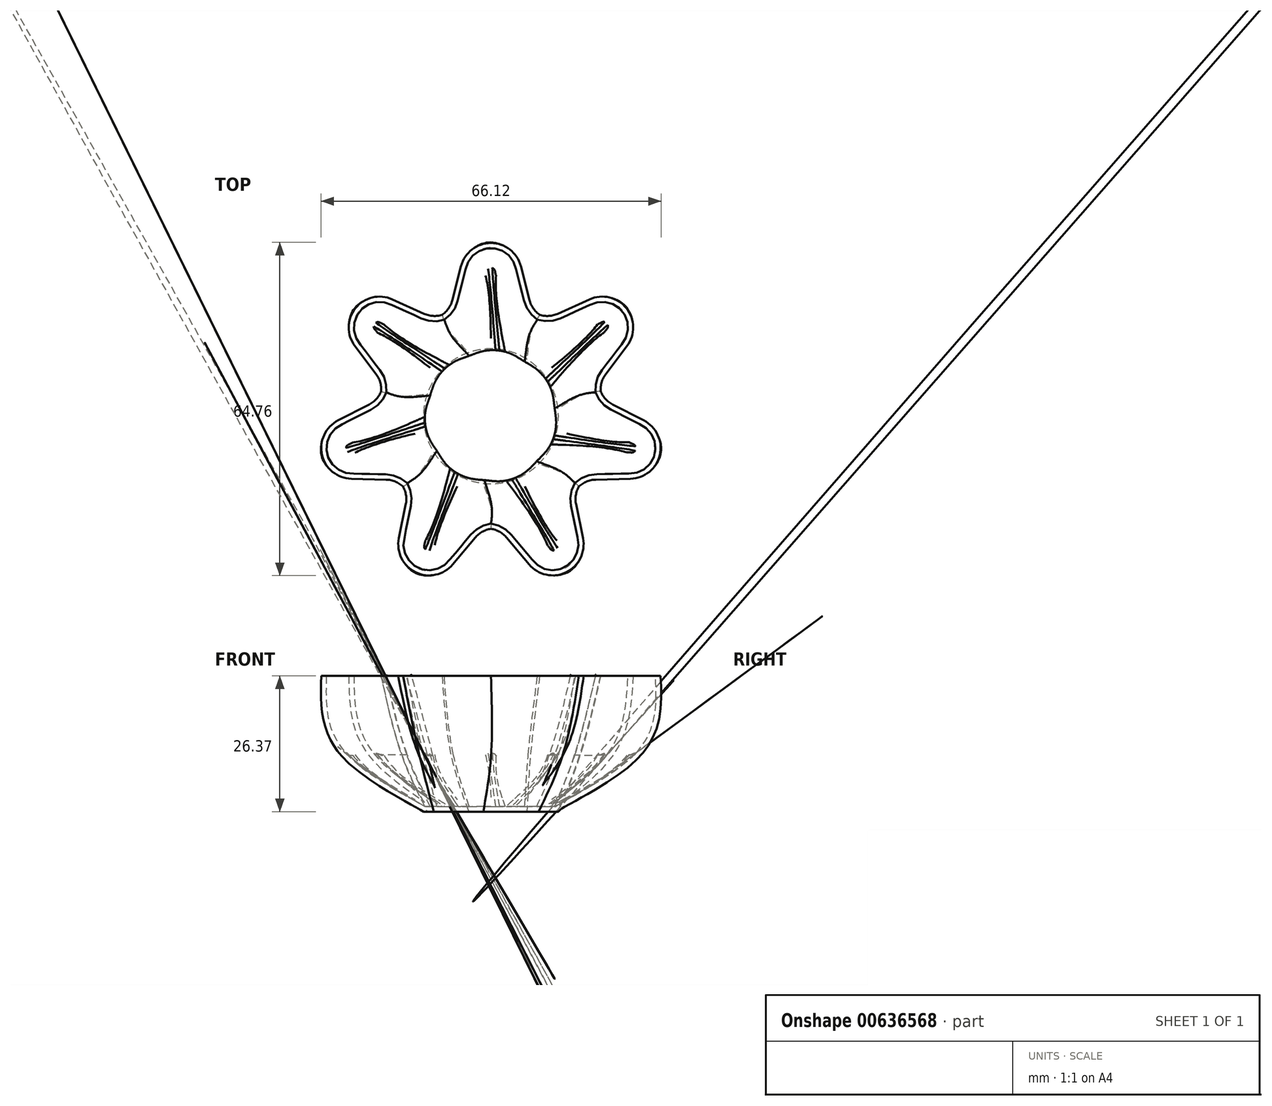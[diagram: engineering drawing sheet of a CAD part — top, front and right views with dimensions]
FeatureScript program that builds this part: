
annotation { "Feature Type Name" : "Feature", "Feature Type Description" : "" }
export const myFeature = defineFeature(function(context is Context, id is Id, definition is map)
    precondition{}
    {
        {
            var Q0;
            Q0=qCreatedBy(makeId("Top.planeOp"),FACE);
            var sketch = newSketch(context, id + "F0", { "sketchPlane" : qUnion([Q0])});
            skLineSegment(sketch, "E0", {"start": v(-7.48, 22.6) * mm, "end": v(-5.82, 29.15) * mm});
            skLineSegment(sketch, "E1.MirrorCS", {"start": v(7.48, 22.6) * mm, "end": v(5.82, 29.15) * mm});
            skPoint(sketch, "E2.visualSharp", {"position": v(0, 52.07) * mm});
            skArc(sketch, "E2.filletArc", {"start": v(5.82, 29.15) * mm, "mid": v(0, 33.67) * mm, "end": v(-5.82, 29.15) * mm});
            skPoint(sketch, "E3.visualSharp", {"position": v(8.06, 20.28) * mm});
            skArc(sketch, "E3.filletArc", {"start": v(7.48, 22.6) * mm, "mid": v(8.22, 20.97) * mm, "end": v(9.5, 19.7) * mm});
            skPoint(sketch, "E4.visualSharp", {"position": v(-8.06, 20.28) * mm});
            skArc(sketch, "E4.filletArc", {"start": v(-9.5, 19.7) * mm, "mid": v(-8.22, 20.97) * mm, "end": v(-7.48, 22.6) * mm});
            skArc(sketch, "E5.1.0", {"start": v(-19.16, 22.72) * mm, "mid": v(-26.32, 21) * mm, "end": v(-26.41, 13.62) * mm});
            skArc(sketch, "E5.1.1", {"start": v(-13, 19.94) * mm, "mid": v(-11.27, 19.5) * mm, "end": v(-9.5, 19.7) * mm});
            skArc(sketch, "E5.1.2", {"start": v(-21.33, 4.87) * mm, "mid": v(-21.52, 6.65) * mm, "end": v(-22.33, 8.25) * mm});
            skLineSegment(sketch, "E5.1.3", {"start": v(-22.33, 8.25) * mm, "end": v(-26.41, 13.62) * mm});
            skLineSegment(sketch, "E5.1.4", {"start": v(-13, 19.94) * mm, "end": v(-19.16, 22.72) * mm});
            skArc(sketch, "E5.2.0", {"start": v(-29.7, -0.82) * mm, "mid": v(-32.83, -7.5) * mm, "end": v(-27.12, -12.16) * mm});
            skArc(sketch, "E5.2.1", {"start": v(-23.7, 2.26) * mm, "mid": v(-22.27, 3.35) * mm, "end": v(-21.33, 4.87) * mm});
            skArc(sketch, "E5.2.2", {"start": v(-17.1, -13.64) * mm, "mid": v(-18.62, -12.68) * mm, "end": v(-20.37, -12.32) * mm});
            skLineSegment(sketch, "E5.2.3", {"start": v(-20.37, -12.32) * mm, "end": v(-27.12, -12.16) * mm});
            skLineSegment(sketch, "E5.2.4", {"start": v(-23.7, 2.26) * mm, "end": v(-29.7, -0.82) * mm});
            skArc(sketch, "E5.3.0", {"start": v(-17.89, -23.74) * mm, "mid": v(-14.6, -30.34) * mm, "end": v(-7.4, -28.78) * mm});
            skArc(sketch, "E5.3.1", {"start": v(-16.54, -17.12) * mm, "mid": v(-16.5, -15.33) * mm, "end": v(-17.1, -13.64) * mm});
            skArc(sketch, "E5.3.2", {"start": v(0, -21.87) * mm, "mid": v(-1.7, -22.46) * mm, "end": v(-3.07, -23.6) * mm});
            skLineSegment(sketch, "E5.3.3", {"start": v(-3.07, -23.6) * mm, "end": v(-7.4, -28.78) * mm});
            skLineSegment(sketch, "E5.3.4", {"start": v(-16.54, -17.12) * mm, "end": v(-17.89, -23.74) * mm});
            skArc(sketch, "E5.4.0", {"start": v(7.4, -28.78) * mm, "mid": v(14.6, -30.34) * mm, "end": v(17.89, -23.74) * mm});
            skArc(sketch, "E5.4.1", {"start": v(3.07, -23.6) * mm, "mid": v(1.7, -22.46) * mm, "end": v(0, -21.87) * mm});
            skArc(sketch, "E5.4.2", {"start": v(17.1, -13.64) * mm, "mid": v(16.5, -15.33) * mm, "end": v(16.54, -17.12) * mm});
            skLineSegment(sketch, "E5.4.3", {"start": v(16.54, -17.12) * mm, "end": v(17.89, -23.74) * mm});
            skLineSegment(sketch, "E5.4.4", {"start": v(3.07, -23.6) * mm, "end": v(7.4, -28.78) * mm});
            skArc(sketch, "E5.5.0", {"start": v(27.12, -12.16) * mm, "mid": v(32.83, -7.5) * mm, "end": v(29.7, -0.82) * mm});
            skArc(sketch, "E5.5.1", {"start": v(20.37, -12.32) * mm, "mid": v(18.62, -12.68) * mm, "end": v(17.1, -13.64) * mm});
            skArc(sketch, "E5.5.2", {"start": v(21.33, 4.87) * mm, "mid": v(22.27, 3.35) * mm, "end": v(23.7, 2.26) * mm});
            skLineSegment(sketch, "E5.5.3", {"start": v(23.7, 2.26) * mm, "end": v(29.7, -0.82) * mm});
            skLineSegment(sketch, "E5.5.4", {"start": v(20.37, -12.32) * mm, "end": v(27.12, -12.16) * mm});
            skArc(sketch, "E5.6.0", {"start": v(26.41, 13.62) * mm, "mid": v(26.32, 21) * mm, "end": v(19.16, 22.72) * mm});
            skArc(sketch, "E5.6.1", {"start": v(22.33, 8.25) * mm, "mid": v(21.52, 6.65) * mm, "end": v(21.33, 4.87) * mm});
            skArc(sketch, "E5.6.2", {"start": v(9.5, 19.7) * mm, "mid": v(11.27, 19.5) * mm, "end": v(13, 19.94) * mm});
            skLineSegment(sketch, "E5.6.3", {"start": v(13, 19.94) * mm, "end": v(19.16, 22.72) * mm});
            skLineSegment(sketch, "E5.6.4", {"start": v(22.33, 8.25) * mm, "end": v(26.41, 13.62) * mm});
            skPoint(sketch, "E5.center", {"position": v(0, 0) * mm});
            skPoint(sketch, "E6.orphan", {"position": v(0.62, -21.82) * mm});
            skPoint(sketch, "E7.orphan", {"position": v(-0.62, -21.82) * mm});
            skPoint(sketch, "E8.orphan", {"position": v(17.45, -13.12) * mm});
            skPoint(sketch, "E9.orphan", {"position": v(16.67, -14.09) * mm});
            skPoint(sketch, "E10.orphan", {"position": v(21.4, 4.25) * mm});
            skPoint(sketch, "E11.orphan", {"position": v(21.13, 5.46) * mm});
            skPoint(sketch, "E12.orphan", {"position": v(10.03, 19.39) * mm});
            skPoint(sketch, "E13.orphan", {"position": v(8.9, 19.93) * mm});
            skPoint(sketch, "E14.orphan", {"position": v(-8.9, 19.93) * mm});
            skPoint(sketch, "E15.orphan", {"position": v(-10.03, 19.39) * mm});
            skPoint(sketch, "E16.orphan", {"position": v(-16.67, -14.09) * mm});
            skPoint(sketch, "E17.orphan", {"position": v(-17.45, -13.12) * mm});
            skPoint(sketch, "E18.orphan", {"position": v(-21.13, 5.46) * mm});
            skPoint(sketch, "E19.orphan", {"position": v(-21.4, 4.25) * mm});
            skSolve(sketch);
        }
        {
            var Q0;
            Q0=qCreatedBy(makeId("Top.planeOp"),FACE);
            cPlane(context, id + "F1", {"entities" : qUnion([Q0]), "cplaneType" : CPlaneType.OFFSET, "offset" : 26.37 * mm, "oppositeDirection" : true, "width" : 150 * mm, "height" : 150 * mm});
        }
        {
            var Q0;
            Q0=qCreatedBy(id+"F1.planeOp",FACE);
            var sketch = newSketch(context, id + "F2", { "sketchPlane" : qUnion([Q0])});
            skCircle(sketch, "E20", {"center": v(0, 0) * mm, "radius": 13.11 * mm});
            skSolve(sketch);
        }
        {
            var Q0;
            Q0=qCreatedBy(makeId("Top.planeOp"),FACE);
            cPlane(context, id + "F3", {"entities" : qUnion([Q0]), "cplaneType" : CPlaneType.OFFSET, "offset" : 15.82 * mm, "oppositeDirection" : true, "width" : 150 * mm, "height" : 150 * mm});
        }
        {
            var Q0;
            Q0=qCreatedBy(id+"F3.planeOp",FACE);
            var sketch = newSketch(context, id + "F4", { "sketchPlane" : qUnion([Q0])});
            skPoint(sketch, "E21.0", {"position": v(-17.1, -13.64) * mm});
            skPoint(sketch, "E21.1", {"position": v(7.48, 22.6) * mm});
            skPoint(sketch, "E21.2", {"position": v(13, 19.94) * mm});
            skPoint(sketch, "E21.3", {"position": v(27.12, -12.16) * mm});
            skPoint(sketch, "E21.4", {"position": v(10.03, 19.39) * mm});
            skArc(sketch, "E21.5", {"start": v(27.12, -12.16) * mm, "mid": v(32.83, -7.5) * mm, "end": v(29.7, -0.82) * mm});
            skPoint(sketch, "E21.6", {"position": v(21.33, 4.87) * mm});
            skArc(sketch, "E21.7", {"start": v(9.5, 19.7) * mm, "mid": v(11.27, 19.5) * mm, "end": v(13, 19.94) * mm});
            skArc(sketch, "E21.8", {"start": v(-13, 19.94) * mm, "mid": v(-11.27, 19.5) * mm, "end": v(-9.5, 19.7) * mm});
            skLineSegment(sketch, "E21.9", {"start": v(20.37, -12.32) * mm, "end": v(27.12, -12.16) * mm});
            skPoint(sketch, "E21.10", {"position": v(-29.7, -0.82) * mm});
            skPoint(sketch, "E21.11", {"position": v(7.4, -28.78) * mm});
            skPoint(sketch, "E21.13", {"position": v(-13, 19.94) * mm});
            skPoint(sketch, "E21.14", {"position": v(-12, -24.93) * mm});
            skArc(sketch, "E21.15", {"start": v(3.07, -23.6) * mm, "mid": v(1.7, -22.46) * mm, "end": v(0, -21.87) * mm});
            skPoint(sketch, "E21.16", {"position": v(-12.32, 23.83) * mm});
            skPoint(sketch, "E21.17", {"position": v(-26.98, -6.16) * mm});
            skArc(sketch, "E21.18", {"start": v(-17.1, -13.64) * mm, "mid": v(-18.62, -12.68) * mm, "end": v(-20.37, -12.32) * mm});
            skPoint(sketch, "E21.19", {"position": v(-3.07, -23.6) * mm});
            skPoint(sketch, "E21.20", {"position": v(23.7, 2.26) * mm});
            skPoint(sketch, "E21.21", {"position": v(21.63, 17.25) * mm});
            skPoint(sketch, "E21.22", {"position": v(16.67, -14.09) * mm});
            skPoint(sketch, "E21.23", {"position": v(0.62, -21.82) * mm});
            skPoint(sketch, "E21.24", {"position": v(-26.41, 13.62) * mm});
            skLineSegment(sketch, "E21.25", {"start": v(-7.48, 22.6) * mm, "end": v(-5.82, 29.15) * mm});
            skPoint(sketch, "E21.26", {"position": v(20.37, -12.32) * mm});
            skPoint(sketch, "E21.27", {"position": v(8.06, 20.28) * mm});
            skPoint(sketch, "E21.28", {"position": v(-21.13, 5.46) * mm});
            skLineSegment(sketch, "E21.29", {"start": v(-3.07, -23.6) * mm, "end": v(-7.4, -28.78) * mm});
            skPoint(sketch, "E21.30", {"position": v(-20.37, -12.32) * mm});
            skPoint(sketch, "E21.31", {"position": v(-17.1, -13.64) * mm});
            skPoint(sketch, "E21.32", {"position": v(22.33, 8.25) * mm});
            skPoint(sketch, "E21.33", {"position": v(26.98, -6.16) * mm});
            skPoint(sketch, "E21.34", {"position": v(-17.89, -23.74) * mm});
            skArc(sketch, "E21.35", {"start": v(21.33, 4.87) * mm, "mid": v(22.27, 3.35) * mm, "end": v(23.7, 2.26) * mm});
            skLineSegment(sketch, "E21.36", {"start": v(22.33, 8.25) * mm, "end": v(26.41, 13.62) * mm});
            skPoint(sketch, "E21.37", {"position": v(-5.82, 29.15) * mm});
            skArc(sketch, "E21.38", {"start": v(22.33, 8.25) * mm, "mid": v(21.52, 6.65) * mm, "end": v(21.33, 4.87) * mm});
            skPoint(sketch, "E21.39", {"position": v(-23.7, 2.26) * mm});
            skPoint(sketch, "E21.40", {"position": v(3.07, -23.6) * mm});
            skPoint(sketch, "E21.41", {"position": v(7.4, -28.78) * mm});
            skLineSegment(sketch, "E21.42", {"start": v(7.48, 22.6) * mm, "end": v(5.82, 29.15) * mm});
            skPoint(sketch, "E21.43", {"position": v(0.76, -26.82) * mm});
            skPoint(sketch, "E21.44", {"position": v(-10.03, 19.39) * mm});
            skPoint(sketch, "E21.45", {"position": v(16.54, -17.12) * mm});
            skPoint(sketch, "E21.46", {"position": v(9.5, 19.7) * mm});
            skPoint(sketch, "E21.47", {"position": v(-21.33, 4.87) * mm});
            skPoint(sketch, "E21.48", {"position": v(-16.54, -17.12) * mm});
            skPoint(sketch, "E21.49", {"position": v(20.37, -12.32) * mm});
            skPoint(sketch, "E21.50", {"position": v(13, 19.94) * mm});
            skPoint(sketch, "E21.51", {"position": v(21.13, 5.46) * mm});
            skArc(sketch, "E21.52", {"start": v(-21.33, 4.87) * mm, "mid": v(-21.52, 6.65) * mm, "end": v(-22.33, 8.25) * mm});
            skLineSegment(sketch, "E21.53", {"start": v(3.07, -23.6) * mm, "end": v(7.4, -28.78) * mm});
            skPoint(sketch, "E21.54", {"position": v(22.33, 8.25) * mm});
            skPoint(sketch, "E21.55", {"position": v(-19.16, 22.72) * mm});
            skLineSegment(sketch, "E21.56.0", {"start": v(17.89, -23.74) * mm, "end": v(16.54, -17.12) * mm});
            skArc(sketch, "E21.56.1", {"start": v(16.54, -17.12) * mm, "mid": v(16.5, -15.33) * mm, "end": v(17.1, -13.64) * mm});
            skArc(sketch, "E21.56.2", {"start": v(17.1, -13.64) * mm, "mid": v(18.62, -12.68) * mm, "end": v(20.37, -12.32) * mm});
            skLineSegment(sketch, "E21.56.3", {"start": v(20.37, -12.32) * mm, "end": v(27.12, -12.16) * mm});
            skArc(sketch, "E21.56.4", {"start": v(27.12, -12.16) * mm, "mid": v(32.83, -7.5) * mm, "end": v(29.7, -0.82) * mm});
            skLineSegment(sketch, "E21.56.5", {"start": v(29.7, -0.82) * mm, "end": v(23.7, 2.26) * mm});
            skArc(sketch, "E21.56.6", {"start": v(23.7, 2.26) * mm, "mid": v(22.27, 3.35) * mm, "end": v(21.33, 4.87) * mm});
            skArc(sketch, "E21.56.7", {"start": v(21.33, 4.87) * mm, "mid": v(21.52, 6.65) * mm, "end": v(22.33, 8.25) * mm});
            skLineSegment(sketch, "E21.56.8", {"start": v(22.33, 8.25) * mm, "end": v(26.41, 13.62) * mm});
            skArc(sketch, "E21.56.9", {"start": v(26.41, 13.62) * mm, "mid": v(26.32, 21) * mm, "end": v(19.16, 22.72) * mm});
            skLineSegment(sketch, "E21.56.10", {"start": v(19.16, 22.72) * mm, "end": v(13, 19.94) * mm});
            skArc(sketch, "E21.56.11", {"start": v(13, 19.94) * mm, "mid": v(11.27, 19.5) * mm, "end": v(9.5, 19.7) * mm});
            skArc(sketch, "E21.56.12", {"start": v(9.5, 19.7) * mm, "mid": v(8.22, 20.97) * mm, "end": v(7.48, 22.6) * mm});
            skLineSegment(sketch, "E21.56.13", {"start": v(7.48, 22.6) * mm, "end": v(5.82, 29.15) * mm});
            skArc(sketch, "E21.56.14", {"start": v(5.82, 29.15) * mm, "mid": v(0, 33.67) * mm, "end": v(-5.82, 29.15) * mm});
            skLineSegment(sketch, "E21.56.15", {"start": v(-5.82, 29.15) * mm, "end": v(-7.48, 22.6) * mm});
            skArc(sketch, "E21.56.16", {"start": v(-7.48, 22.6) * mm, "mid": v(-8.22, 20.97) * mm, "end": v(-9.5, 19.7) * mm});
            skArc(sketch, "E21.56.17", {"start": v(-9.5, 19.7) * mm, "mid": v(-11.27, 19.5) * mm, "end": v(-13, 19.94) * mm});
            skLineSegment(sketch, "E21.56.18", {"start": v(-13, 19.94) * mm, "end": v(-19.16, 22.72) * mm});
            skArc(sketch, "E21.56.19", {"start": v(-19.16, 22.72) * mm, "mid": v(-26.32, 21) * mm, "end": v(-26.41, 13.62) * mm});
            skLineSegment(sketch, "E21.56.20", {"start": v(-26.41, 13.62) * mm, "end": v(-22.33, 8.25) * mm});
            skArc(sketch, "E21.56.21", {"start": v(-22.33, 8.25) * mm, "mid": v(-21.52, 6.65) * mm, "end": v(-21.33, 4.87) * mm});
            skArc(sketch, "E21.56.22", {"start": v(-21.33, 4.87) * mm, "mid": v(-22.27, 3.35) * mm, "end": v(-23.7, 2.26) * mm});
            skLineSegment(sketch, "E21.56.23", {"start": v(-23.7, 2.26) * mm, "end": v(-29.7, -0.82) * mm});
            skArc(sketch, "E21.56.24", {"start": v(-29.7, -0.82) * mm, "mid": v(-32.83, -7.5) * mm, "end": v(-27.12, -12.16) * mm});
            skLineSegment(sketch, "E21.56.25", {"start": v(-27.12, -12.16) * mm, "end": v(-20.37, -12.32) * mm});
            skArc(sketch, "E21.56.26", {"start": v(-20.37, -12.32) * mm, "mid": v(-18.62, -12.68) * mm, "end": v(-17.1, -13.64) * mm});
            skArc(sketch, "E21.56.27", {"start": v(-17.1, -13.64) * mm, "mid": v(-16.5, -15.33) * mm, "end": v(-16.54, -17.12) * mm});
            skLineSegment(sketch, "E21.56.28", {"start": v(-16.54, -17.12) * mm, "end": v(-17.89, -23.74) * mm});
            skArc(sketch, "E21.56.29", {"start": v(-17.89, -23.74) * mm, "mid": v(-14.6, -30.34) * mm, "end": v(-7.4, -28.78) * mm});
            skLineSegment(sketch, "E21.56.30", {"start": v(-7.4, -28.78) * mm, "end": v(-3.07, -23.6) * mm});
            skArc(sketch, "E21.56.31", {"start": v(-3.07, -23.6) * mm, "mid": v(-1.7, -22.46) * mm, "end": v(0, -21.87) * mm});
            skArc(sketch, "E21.56.32", {"start": v(0, -21.87) * mm, "mid": v(1.7, -22.46) * mm, "end": v(3.07, -23.6) * mm});
            skLineSegment(sketch, "E21.56.33", {"start": v(3.07, -23.6) * mm, "end": v(7.4, -28.78) * mm});
            skArc(sketch, "E21.56.34", {"start": v(7.4, -28.78) * mm, "mid": v(14.6, -30.34) * mm, "end": v(17.89, -23.74) * mm});
            skPoint(sketch, "E21.57", {"position": v(-17.89, -23.74) * mm});
            skPoint(sketch, "E21.58", {"position": v(21.33, 4.87) * mm});
            skPoint(sketch, "E21.59", {"position": v(7.48, 22.6) * mm});
            skPoint(sketch, "E21.60", {"position": v(-8.06, 20.28) * mm});
            skPoint(sketch, "E21.61", {"position": v(-20.49, -17.32) * mm});
            skArc(sketch, "E21.62", {"start": v(7.4, -28.78) * mm, "mid": v(14.6, -30.34) * mm, "end": v(17.89, -23.74) * mm});
            skArc(sketch, "E21.63", {"start": v(5.82, 29.15) * mm, "mid": v(0, 33.67) * mm, "end": v(-5.82, 29.15) * mm});
            skPoint(sketch, "E21.64", {"position": v(0, 0) * mm});
            skPoint(sketch, "E21.65", {"position": v(-26.31, 5.22) * mm});
            skPoint(sketch, "E21.66", {"position": v(-23.7, 2.26) * mm});
            skPoint(sketch, "E21.67", {"position": v(-3.07, -23.6) * mm});
            skPoint(sketch, "E21.68", {"position": v(-9.5, 19.7) * mm});
            skPoint(sketch, "E21.69", {"position": v(0, 52.07) * mm});
            skPoint(sketch, "E21.70", {"position": v(23.7, 2.26) * mm});
            skPoint(sketch, "E21.71", {"position": v(25.97, 6.71) * mm});
            skPoint(sketch, "E21.72", {"position": v(17.45, -13.12) * mm});
            skPoint(sketch, "E21.73", {"position": v(-9.5, 19.7) * mm});
            skLineSegment(sketch, "E21.74", {"start": v(-22.33, 8.25) * mm, "end": v(-26.41, 13.62) * mm});
            skPoint(sketch, "E21.75", {"position": v(0, 0) * mm});
            skPoint(sketch, "E21.76", {"position": v(-7.48, 22.6) * mm});
            skPoint(sketch, "E21.77", {"position": v(-22.33, 8.25) * mm});
            skPoint(sketch, "E21.78", {"position": v(17.1, -13.64) * mm});
            skPoint(sketch, "E21.79", {"position": v(29.7, -0.82) * mm});
            skPoint(sketch, "E21.80", {"position": v(5.82, 29.15) * mm});
            skPoint(sketch, "E21.81", {"position": v(-0.76, -26.82) * mm});
            skLineSegment(sketch, "E21.82", {"start": v(-20.37, -12.32) * mm, "end": v(-27.12, -12.16) * mm});
            skArc(sketch, "E21.83", {"start": v(0, -21.87) * mm, "mid": v(-1.7, -22.46) * mm, "end": v(-3.07, -23.6) * mm});
            skPoint(sketch, "E21.84", {"position": v(-17.45, -13.12) * mm});
            skPoint(sketch, "E21.85", {"position": v(0, 27.67) * mm});
            skPoint(sketch, "E21.86", {"position": v(0, 0) * mm});
            skArc(sketch, "E21.87", {"start": v(7.48, 22.6) * mm, "mid": v(8.22, 20.97) * mm, "end": v(9.5, 19.7) * mm});
            skPoint(sketch, "E21.88", {"position": v(-16.54, -17.12) * mm});
            skPoint(sketch, "E21.89", {"position": v(-20.37, -12.32) * mm});
            skPoint(sketch, "E21.90", {"position": v(26.41, 13.62) * mm});
            skPoint(sketch, "E21.91", {"position": v(19.16, 22.72) * mm});
            skPoint(sketch, "E21.92", {"position": v(21.44, -16.12) * mm});
            skPoint(sketch, "E21.93", {"position": v(-29.7, -0.82) * mm});
            skPoint(sketch, "E21.94", {"position": v(8.9, 19.93) * mm});
            skArc(sketch, "E21.95", {"start": v(20.37, -12.32) * mm, "mid": v(18.62, -12.68) * mm, "end": v(17.1, -13.64) * mm});
            skLineSegment(sketch, "E21.96", {"start": v(13, 19.94) * mm, "end": v(19.16, 22.72) * mm});
            skPoint(sketch, "E21.97", {"position": v(-7.48, 22.6) * mm});
            skArc(sketch, "E21.98", {"start": v(26.41, 13.62) * mm, "mid": v(26.32, 21) * mm, "end": v(19.16, 22.72) * mm});
            skPoint(sketch, "E21.99", {"position": v(-27.12, -12.16) * mm});
            skLineSegment(sketch, "E21.100", {"start": v(-13, 19.94) * mm, "end": v(-19.16, 22.72) * mm});
            skPoint(sketch, "E21.101", {"position": v(3.07, -23.6) * mm});
            skPoint(sketch, "E21.102", {"position": v(17.89, -23.74) * mm});
            skPoint(sketch, "E21.103", {"position": v(-21.33, 4.87) * mm});
            skPoint(sketch, "E21.104", {"position": v(-21.63, 17.25) * mm});
            skPoint(sketch, "E21.105", {"position": v(-21.44, -16.12) * mm});
            skPoint(sketch, "E21.106", {"position": v(-8.9, 19.93) * mm});
            skPoint(sketch, "E21.107", {"position": v(16.54, -17.12) * mm});
            skPoint(sketch, "E21.108", {"position": v(5.82, 29.15) * mm});
            skArc(sketch, "E21.109", {"start": v(17.1, -13.64) * mm, "mid": v(16.5, -15.33) * mm, "end": v(16.54, -17.12) * mm});
            skLineSegment(sketch, "E21.110", {"start": v(-23.7, 2.26) * mm, "end": v(-29.7, -0.82) * mm});
            skPoint(sketch, "E21.111", {"position": v(-7.4, -28.78) * mm});
            skArc(sketch, "E21.112", {"start": v(-9.5, 19.7) * mm, "mid": v(-8.22, 20.97) * mm, "end": v(-7.48, 22.6) * mm});
            skPoint(sketch, "E21.113", {"position": v(9.5, 19.7) * mm});
            skPoint(sketch, "E21.114", {"position": v(29.7, -0.82) * mm});
            skPoint(sketch, "E21.115", {"position": v(26.31, 5.22) * mm});
            skPoint(sketch, "E21.116", {"position": v(21.4, 4.25) * mm});
            skLineSegment(sketch, "E21.117", {"start": v(16.54, -17.12) * mm, "end": v(17.89, -23.74) * mm});
            skPoint(sketch, "E21.118", {"position": v(19.16, 22.72) * mm});
            skPoint(sketch, "E21.119", {"position": v(-19.16, 22.72) * mm});
            skPoint(sketch, "E21.120", {"position": v(-13, 19.94) * mm});
            skPoint(sketch, "E21.121", {"position": v(17.1, -13.64) * mm});
            skPoint(sketch, "E21.122", {"position": v(-22.33, 8.25) * mm});
            skPoint(sketch, "E21.123", {"position": v(-25.97, 6.71) * mm});
            skArc(sketch, "E21.124", {"start": v(-29.7, -0.82) * mm, "mid": v(-32.83, -7.5) * mm, "end": v(-27.12, -12.16) * mm});
            skPoint(sketch, "E21.125", {"position": v(12.32, 23.83) * mm});
            skPoint(sketch, "E21.126", {"position": v(-21.4, 4.25) * mm});
            skLineSegment(sketch, "E21.127", {"start": v(-16.54, -17.12) * mm, "end": v(-17.89, -23.74) * mm});
            skPoint(sketch, "E21.129", {"position": v(-10.95, 24.5) * mm});
            skArc(sketch, "E21.130", {"start": v(-17.89, -23.74) * mm, "mid": v(-14.6, -30.34) * mm, "end": v(-7.4, -28.78) * mm});
            skPoint(sketch, "E21.131", {"position": v(-5.82, 29.15) * mm});
            skPoint(sketch, "E21.132", {"position": v(0, -21.87) * mm});
            skPoint(sketch, "E21.133", {"position": v(-27.12, -12.16) * mm});
            skPoint(sketch, "E21.134", {"position": v(26.41, 13.62) * mm});
            skPoint(sketch, "E21.135", {"position": v(-0.62, -21.82) * mm});
            skPoint(sketch, "E21.136", {"position": v(-7.4, -28.78) * mm});
            skArc(sketch, "E21.137", {"start": v(-19.16, 22.72) * mm, "mid": v(-26.32, 21) * mm, "end": v(-26.41, 13.62) * mm});
            skPoint(sketch, "E21.138", {"position": v(20.49, -17.32) * mm});
            skLineSegment(sketch, "E21.139", {"start": v(23.7, 2.26) * mm, "end": v(29.7, -0.82) * mm});
            skPoint(sketch, "E21.140", {"position": v(10.95, 24.5) * mm});
            skPoint(sketch, "E21.141", {"position": v(-26.41, 13.62) * mm});
            skPoint(sketch, "E21.142", {"position": v(27.12, -12.16) * mm});
            skPoint(sketch, "E21.143", {"position": v(0, -21.87) * mm});
            skPoint(sketch, "E21.144", {"position": v(12, -24.93) * mm});
            skPoint(sketch, "E21.145", {"position": v(-16.67, -14.09) * mm});
            skPoint(sketch, "E21.146", {"position": v(17.89, -23.74) * mm});
            skArc(sketch, "E21.147", {"start": v(-16.54, -17.12) * mm, "mid": v(-16.5, -15.33) * mm, "end": v(-17.1, -13.64) * mm});
            skArc(sketch, "E21.148", {"start": v(-23.7, 2.26) * mm, "mid": v(-22.27, 3.35) * mm, "end": v(-21.33, 4.87) * mm});
            skLineSegment(sketch, "E22.0", {"start": v(3.4, 21.57) * mm, "end": v(1.74, 28.11) * mm});
            skArc(sketch, "E22.1", {"start": v(3.4, 21.57) * mm, "mid": v(4.96, 18.3) * mm, "end": v(7.66, 15.9) * mm});
            skArc(sketch, "E22.2", {"start": v(7.66, 15.9) * mm, "mid": v(11.22, 15.3) * mm, "end": v(14.74, 16.1) * mm});
            skLineSegment(sketch, "E22.3", {"start": v(14.74, 16.1) * mm, "end": v(20.9, 18.9) * mm});
            skArc(sketch, "E22.4", {"start": v(23.07, 16.16) * mm, "mid": v(23.04, 18.37) * mm, "end": v(20.9, 18.9) * mm});
            skLineSegment(sketch, "E22.5", {"start": v(18.98, 10.78) * mm, "end": v(23.07, 16.16) * mm});
            skArc(sketch, "E22.6", {"start": v(18.98, 10.78) * mm, "mid": v(17.4, 7.53) * mm, "end": v(17.2, 3.93) * mm});
            skArc(sketch, "E22.7", {"start": v(17.2, 3.93) * mm, "mid": v(18.95, 0.77) * mm, "end": v(21.78, -1.48) * mm});
            skLineSegment(sketch, "E22.8", {"start": v(21.78, -1.48) * mm, "end": v(27.8, -4.55) * mm});
            skArc(sketch, "E22.9", {"start": v(27.02, -7.96) * mm, "mid": v(28.73, -6.56) * mm, "end": v(27.8, -4.55) * mm});
            skLineSegment(sketch, "E22.10", {"start": v(20.27, -8.12) * mm, "end": v(27.02, -7.96) * mm});
            skArc(sketch, "E22.11", {"start": v(1.74, 28.11) * mm, "mid": v(0, 29.47) * mm, "end": v(-1.74, 28.11) * mm});
            skArc(sketch, "E22.12", {"start": v(20.27, -8.12) * mm, "mid": v(16.74, -8.91) * mm, "end": v(13.8, -11) * mm});
            skArc(sketch, "E22.13", {"start": v(-27.8, -4.55) * mm, "mid": v(-28.73, -6.56) * mm, "end": v(-27.02, -7.96) * mm});
            skLineSegment(sketch, "E22.14", {"start": v(-21.78, -1.48) * mm, "end": v(-27.8, -4.55) * mm});
            skArc(sketch, "E22.15", {"start": v(-17.2, 3.93) * mm, "mid": v(-18.95, 0.77) * mm, "end": v(-21.78, -1.48) * mm});
            skArc(sketch, "E22.16", {"start": v(-17.2, 3.93) * mm, "mid": v(-17.4, 7.53) * mm, "end": v(-18.98, 10.78) * mm});
            skLineSegment(sketch, "E22.17", {"start": v(-23.07, 16.16) * mm, "end": v(-18.98, 10.78) * mm});
            skArc(sketch, "E22.18", {"start": v(-20.9, 18.9) * mm, "mid": v(-23.04, 18.37) * mm, "end": v(-23.07, 16.16) * mm});
            skLineSegment(sketch, "E22.19", {"start": v(-3.4, 21.57) * mm, "end": v(-1.74, 28.11) * mm});
            skArc(sketch, "E22.20", {"start": v(-7.66, 15.9) * mm, "mid": v(-4.96, 18.3) * mm, "end": v(-3.4, 21.57) * mm});
            skArc(sketch, "E22.21", {"start": v(-14.74, 16.1) * mm, "mid": v(-11.22, 15.3) * mm, "end": v(-7.66, 15.9) * mm});
            skLineSegment(sketch, "E22.22", {"start": v(-14.74, 16.1) * mm, "end": v(-20.9, 18.9) * mm});
            skLineSegment(sketch, "E22.23", {"start": v(-20.27, -8.12) * mm, "end": v(-27.02, -7.96) * mm});
            skArc(sketch, "E22.24", {"start": v(-13.8, -11) * mm, "mid": v(-16.74, -8.91) * mm, "end": v(-20.27, -8.12) * mm});
            skArc(sketch, "E22.25", {"start": v(-12.43, -17.95) * mm, "mid": v(-12.42, -14.34) * mm, "end": v(-13.8, -11) * mm});
            skLineSegment(sketch, "E22.26", {"start": v(-12.43, -17.95) * mm, "end": v(-13.77, -24.57) * mm});
            skArc(sketch, "E22.27", {"start": v(-13.77, -24.57) * mm, "mid": v(-12.79, -26.55) * mm, "end": v(-10.63, -26.09) * mm});
            skLineSegment(sketch, "E22.28", {"start": v(-6.29, -20.9) * mm, "end": v(-10.63, -26.09) * mm});
            skArc(sketch, "E22.29", {"start": v(0, -17.65) * mm, "mid": v(-3.47, -18.65) * mm, "end": v(-6.29, -20.9) * mm});
            skArc(sketch, "E22.30", {"start": v(6.29, -20.9) * mm, "mid": v(3.47, -18.65) * mm, "end": v(0, -17.65) * mm});
            skLineSegment(sketch, "E22.31", {"start": v(6.29, -20.9) * mm, "end": v(10.63, -26.09) * mm});
            skArc(sketch, "E22.32", {"start": v(10.63, -26.09) * mm, "mid": v(12.79, -26.55) * mm, "end": v(13.77, -24.57) * mm});
            skLineSegment(sketch, "E22.33", {"start": v(12.43, -17.95) * mm, "end": v(13.77, -24.57) * mm});
            skArc(sketch, "E22.34", {"start": v(13.8, -11) * mm, "mid": v(12.42, -14.34) * mm, "end": v(12.43, -17.95) * mm});
            skSolve(sketch);
        }
        {
            var Q0;
            Q0=makeQuery(id+"F0.imprint","IMPRINT",FACE,{"disambiguationData":[TD([[makeQuery(id+"F0.imprint","IMPRINT",EDGE,{"derivedFrom":sQuery(id+"F0.wireOp",EDGE,"E0")}),-1.0]])]});
            var Q1;
            Q1=makeQuery(id+"F4.imprint","IMPRINT",FACE,{"disambiguationData":[TD([[makeQuery(id+"F4.imprint","IMPRINT",EDGE,{"derivedFrom":sQuery(id+"F4.wireOp",EDGE,"E22.0")}),1.0]])]});
            var Q2;
            Q2=makeQuery(id+"F2.imprint","IMPRINT",FACE,{"disambiguationData":[TD([[makeQuery(id+"F2.imprint","IMPRINT",EDGE,{"derivedFrom":sQuery(id+"F2.wireOp",EDGE,"E20")}),1.0]])]});
            loft(context, id + "F5", {"sheetProfilesArray" : [{ "sheetProfileEntities" : qUnion([Q0]) }, { "sheetProfileEntities" : qUnion([Q1]) }, { "sheetProfileEntities" : qUnion([Q2]) }]});
        }
        {
            var Q0;
            Q0=makeQuery(id+"F5.opLoft","CAP_FACE",FACE,{"disambiguationData":[OSD([makeQuery(id+"F0.imprint","IMPRINT",FACE,{"disambiguationData":[TD([[makeQuery(id+"F0.imprint","IMPRINT",EDGE,{"derivedFrom":sQuery(id+"F0.wireOp",EDGE,"E0")}),-1.0]])]})])],"isStart":true});
            shell(context, id + "F6", {"entities" : qUnion([Q0]), "thickness" : 1 * mm});
        }
    });
